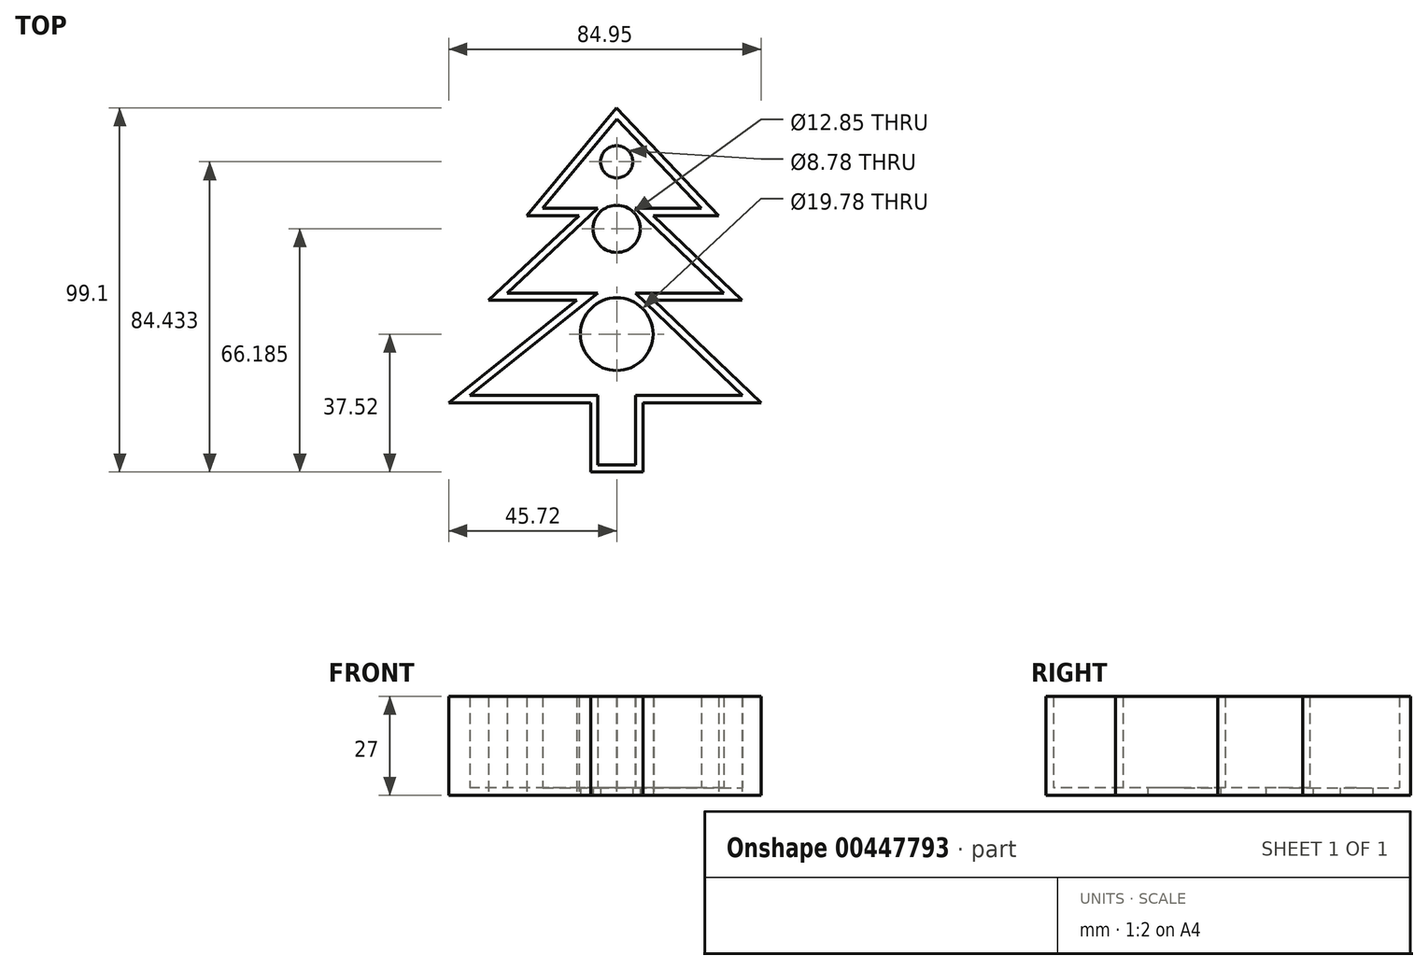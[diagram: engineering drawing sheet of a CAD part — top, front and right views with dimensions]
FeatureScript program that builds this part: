
annotation { "Feature Type Name" : "Feature", "Feature Type Description" : "" }
export const myFeature = defineFeature(function(context is Context, id is Id, definition is map)
    precondition{}
    {
        {
            var Q0;
            Q0=qCreatedBy(makeId("Top.planeOp"),FACE);
            var sketch = newSketch(context, id + "F0", { "sketchPlane" : qUnion([Q0])});
            skLineSegment(sketch, "E0", {"start": v(0, 58.57) * mm, "end": v(-20.16, 34.24) * mm});
            skLineSegment(sketch, "E1", {"start": v(-20.16, 34.24) * mm, "end": v(-5.12, 34.24) * mm});
            skLineSegment(sketch, "E2", {"start": v(-5.12, 34.24) * mm, "end": v(-29.76, 11.2) * mm});
            skLineSegment(sketch, "E3", {"start": v(-29.76, 11.2) * mm, "end": v(-5.12, 11.2) * mm});
            skLineSegment(sketch, "E4", {"start": v(-5.12, 11.2) * mm, "end": v(-40, -16.64) * mm});
            skLineSegment(sketch, "E5", {"start": v(-40, -16.64) * mm, "end": v(-5.12, -16.64) * mm});
            skLineSegment(sketch, "E6", {"start": v(-5.12, -16.64) * mm, "end": v(-5.12, -35.52) * mm});
            skLineSegment(sketch, "E7", {"start": v(-5.12, -35.52) * mm, "end": v(5.12, -35.52) * mm});
            skLineSegment(sketch, "E8", {"start": v(5.12, -35.52) * mm, "end": v(5.12, -16.64) * mm});
            skLineSegment(sketch, "E9", {"start": v(5.12, -16.64) * mm, "end": v(34.24, -16.64) * mm});
            skLineSegment(sketch, "E10", {"start": v(34.24, -16.64) * mm, "end": v(5.12, 11.2) * mm});
            skLineSegment(sketch, "E11", {"start": v(5.12, 11.2) * mm, "end": v(29.12, 11.2) * mm});
            skLineSegment(sketch, "E12", {"start": v(29.12, 11.2) * mm, "end": v(5.02, 34.24) * mm});
            skLineSegment(sketch, "E13", {"start": v(5.02, 34.24) * mm, "end": v(23.04, 34.24) * mm});
            skLineSegment(sketch, "E14", {"start": v(23.04, 34.24) * mm, "end": v(0, 58.57) * mm});
            skSolve(sketch);
        }
        {
            var Q0;
            Q0 = qSketchRegion(id + "F0", true);
            extrude(context, id + "F1", {"entities" : qUnion([Q0]), "depth" : 25 * mm});
        }
        {
            var Q0;
            Q0=makeQuery(id+"F1.opExtrude","CAP_FACE",FACE,{"disambiguationData":[OSD([sQuery(id+"F0.wireOp",EDGE,"E0"),sQuery(id+"F0.wireOp",EDGE,"E1"),sQuery(id+"F0.wireOp",EDGE,"E2"),sQuery(id+"F0.wireOp",EDGE,"E3"),sQuery(id+"F0.wireOp",EDGE,"E4"),sQuery(id+"F0.wireOp",EDGE,"E5"),sQuery(id+"F0.wireOp",EDGE,"E6"),sQuery(id+"F0.wireOp",EDGE,"E7"),sQuery(id+"F0.wireOp",EDGE,"E8"),sQuery(id+"F0.wireOp",EDGE,"E9"),sQuery(id+"F0.wireOp",EDGE,"E10"),sQuery(id+"F0.wireOp",EDGE,"E11"),sQuery(id+"F0.wireOp",EDGE,"E12"),sQuery(id+"F0.wireOp",EDGE,"E13"),sQuery(id+"F0.wireOp",EDGE,"E14")])],"isStart":false});
            shell(context, id + "F2", {"entities" : qUnion([Q0]), "thickness" : 2 * mm, "oppositeDirection" : true});
        }
        {
            var Q0;
            Q0=makeQuery(id+"F1.opExtrude","CAP_FACE",FACE,{"disambiguationData":[OSD([sQuery(id+"F0.wireOp",EDGE,"E0"),sQuery(id+"F0.wireOp",EDGE,"E1"),sQuery(id+"F0.wireOp",EDGE,"E2"),sQuery(id+"F0.wireOp",EDGE,"E3"),sQuery(id+"F0.wireOp",EDGE,"E4"),sQuery(id+"F0.wireOp",EDGE,"E5"),sQuery(id+"F0.wireOp",EDGE,"E6"),sQuery(id+"F0.wireOp",EDGE,"E7"),sQuery(id+"F0.wireOp",EDGE,"E8"),sQuery(id+"F0.wireOp",EDGE,"E9"),sQuery(id+"F0.wireOp",EDGE,"E10"),sQuery(id+"F0.wireOp",EDGE,"E11"),sQuery(id+"F0.wireOp",EDGE,"E12"),sQuery(id+"F0.wireOp",EDGE,"E13"),sQuery(id+"F0.wireOp",EDGE,"E14")])],"isStart":true});
            var sketch = newSketch(context, id + "F3", { "sketchPlane" : qUnion([Q0])});
            skCircle(sketch, "E15", {"center": v(0, 0) * mm, "radius": 9.9 * mm});
            skCircle(sketch, "E16", {"center": v(0, -28.67) * mm, "radius": 6.42 * mm});
            skCircle(sketch, "E17", {"center": v(0, -46.91) * mm, "radius": 4.39 * mm});
            skPoint(sketch, "E17.centerSnap0", {"position": v(-12.26, -46.91) * mm});
            skSolve(sketch);
        }
        {
            var Q0;
            Q0=makeQuery(id+"F3.imprint","IMPRINT",FACE,{"disambiguationData":[TD([[makeQuery(id+"F3.imprint","IMPRINT",EDGE,{"derivedFrom":sQuery(id+"F3.wireOp",EDGE,"E15")}),1.0]])]});
            var Q1;
            Q1=makeQuery(id+"F3.imprint","IMPRINT",FACE,{"disambiguationData":[TD([[makeQuery(id+"F3.imprint","IMPRINT",EDGE,{"derivedFrom":sQuery(id+"F3.wireOp",EDGE,"E17")}),1.0]])]});
            var Q2;
            Q2=makeQuery(id+"F3.imprint","IMPRINT",FACE,{"disambiguationData":[TD([[makeQuery(id+"F3.imprint","IMPRINT",EDGE,{"derivedFrom":sQuery(id+"F3.wireOp",EDGE,"E16")}),1.0]])]});
            var Q3;
            Q3=sQuery(id+"F3.wireOp",EDGE,"E15");
            var Q4;
            Q4=sQuery(id+"F3.wireOp",EDGE,"E16");
            var Q5;
            Q5=sQuery(id+"F3.wireOp",EDGE,"E17");
            extrude(context, id + "F4", {"entities" : qUnion([Q0, Q1, Q2]), "operationType" : NewBodyOperationType.REMOVE, "surfaceEntities" : qUnion([Q3, Q4, Q5]), "oppositeDirection" : true, "depth" : 25 * mm});
        }
    });
